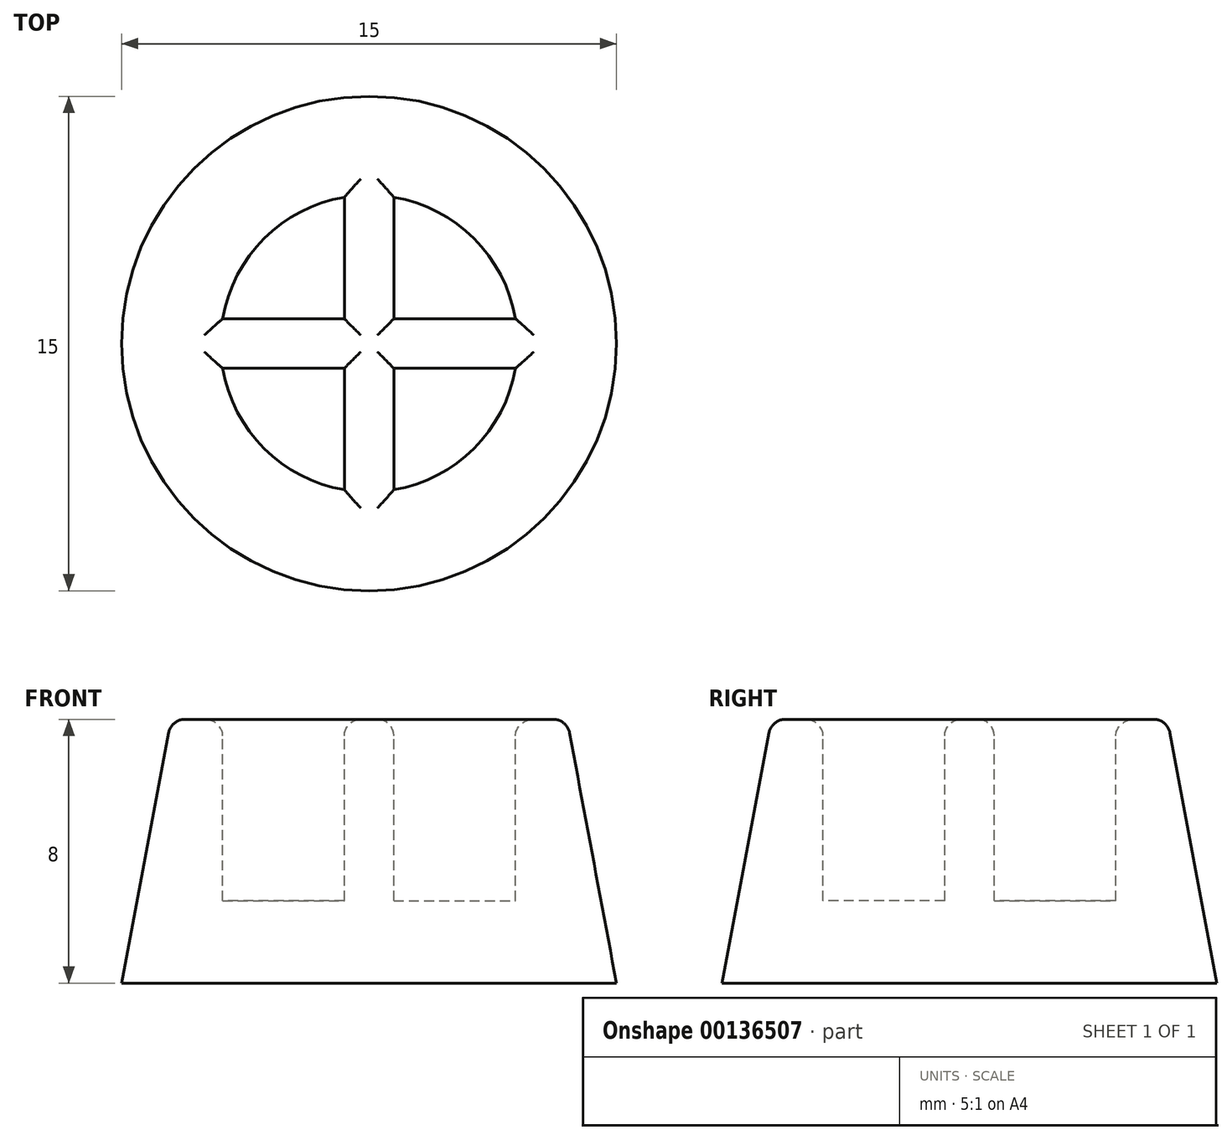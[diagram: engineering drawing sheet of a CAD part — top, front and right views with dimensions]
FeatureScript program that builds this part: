
annotation { "Feature Type Name" : "Feature", "Feature Type Description" : "" }
export const myFeature = defineFeature(function(context is Context, id is Id, definition is map)
    precondition{}
    {
        {
            var Q0;
            Q0=qCreatedBy(makeId("Front.planeOp"),FACE);
            var sketch = newSketch(context, id + "F0", { "sketchPlane" : qUnion([Q0])});
            skLineSegment(sketch, "E0", {"start": v(0, 0) * mm, "end": v(7.5, 0) * mm});
            skLineSegment(sketch, "E1", {"start": v(7.5, 0) * mm, "end": v(6, 8) * mm});
            skLineSegment(sketch, "E2", {"start": v(6, 8) * mm, "end": v(4.5, 8) * mm});
            skLineSegment(sketch, "E3", {"start": v(4.5, 8) * mm, "end": v(4.5, 2.5) * mm});
            skLineSegment(sketch, "E4", {"start": v(4.5, 2.5) * mm, "end": v(0, 2.5) * mm});
            skLineSegment(sketch, "E5", {"start": v(0, 2.5) * mm, "end": v(0, 0) * mm});
            skSolve(sketch);
        }
        {
            var Q0;
            Q0 = qSketchRegion(id + "F0", true);
            var Q1;
            Q1=sQuery(id+"F0.wireOp",EDGE,"E5");
            revolve(context, id + "F1", {"entities" : qUnion([Q0]), "axis" : qUnion([Q1]), "revolveType" : RevolveType.FULL});
        }
        {
            var Q0;
            Q0=makeQuery(id+"F1.opRevolve","SWEPT_FACE",FACE,{"disambiguationData":[OSD([sQuery(id+"F0.wireOp",EDGE,"E4")])]});
            var sketch = newSketch(context, id + "F2", { "sketchPlane" : qUnion([Q0])});
            skLineSegment(sketch, "E6", {"start": v(-5, 0.75) * mm, "end": v(-0.75, 0.75) * mm});
            skLineSegment(sketch, "E7", {"start": v(-0.75, 0.75) * mm, "end": v(-0.75, 5) * mm});
            skLineSegment(sketch, "E8", {"start": v(-0.75, 5) * mm, "end": v(0.75, 5) * mm});
            skLineSegment(sketch, "E9", {"start": v(0.75, 5) * mm, "end": v(0.75, 0.75) * mm});
            skLineSegment(sketch, "E10", {"start": v(0.75, 0.75) * mm, "end": v(5, 0.75) * mm});
            skLineSegment(sketch, "E11", {"start": v(5, 0.75) * mm, "end": v(5, -0.75) * mm});
            skLineSegment(sketch, "E12", {"start": v(5, -0.75) * mm, "end": v(0.75, -0.75) * mm});
            skLineSegment(sketch, "E13", {"start": v(0.75, -0.75) * mm, "end": v(0.75, -5) * mm});
            skLineSegment(sketch, "E14", {"start": v(0.75, -5) * mm, "end": v(-0.75, -5) * mm});
            skLineSegment(sketch, "E15", {"start": v(-0.75, -5) * mm, "end": v(-0.75, -0.75) * mm});
            skLineSegment(sketch, "E16", {"start": v(-0.75, -0.75) * mm, "end": v(-5, -0.75) * mm});
            skLineSegment(sketch, "E17", {"start": v(-5, -0.75) * mm, "end": v(-5, 0.75) * mm});
            skLineSegment(sketch, "E18", {"start": v(-0.75, 5) * mm, "end": v(0.75, -5) * mm, "construction": true});
            skLineSegment(sketch, "E19", {"start": v(0.75, 5) * mm, "end": v(-0.75, -5) * mm, "construction": true});
            skPoint(sketch, "E20", {"position": v(0, 0) * mm});
            skSolve(sketch);
        }
        {
            var Q0;
            Q0 = qSketchRegion(id + "F2", true);
            var Q1;
            Q1=makeQuery(id+"F1.opRevolve","SWEPT_FACE",FACE,{"disambiguationData":[OSD([sQuery(id+"F0.wireOp",EDGE,"E2")])]});
            extrude(context, id + "F3", {"entities" : qUnion([Q0]), "operationType" : NewBodyOperationType.ADD, "endBound" : BoundingType.UP_TO_SURFACE, "endBoundEntityFace" : qUnion([Q1]), "depth" : 25 * mm});
        }
        {
            var Q0;
            Q0=makeQuery(id+"F1.opRevolve","SWEPT_EDGE",EDGE,{"disambiguationData":[OSD([sQuery(id+"F0.wireOp",EDGE,"E1"),sQuery(id+"F0.wireOp",EDGE,"E2")])]});
            var Q1;
            Q1=makeQuery(id+"F3.opExtrude","CAP_EDGE",EDGE,{"disambiguationData":[OSD([sQuery(id+"F2.wireOp",EDGE,"E16")])],"isStart":false});
            var Q2;
            Q2=makeQuery(id+"F3.opExtrude","CAP_EDGE",EDGE,{"disambiguationData":[OSD([sQuery(id+"F2.wireOp",EDGE,"E15")])],"isStart":false});
            var Q3;
            {var subQ0=sQuery(id+"F2.wireOp",EDGE,"E15");var subQ2=sQuery(id+"F0.wireOp",EDGE,"E3");var subQ3=sQuery(id+"F0.wireOp",EDGE,"E2");Q3=makeQuery(id+"F3.boolean.opBoolean","SPLIT",EDGE,{"disambiguationData":[TD([makeQuery(id+"F3.opExtrude","SWEPT_FACE",FACE,{"disambiguationData":[OSD([subQ0])]})])],"derivedFrom":makeQuery(id+"F1.opRevolve","SWEPT_EDGE",EDGE,{"disambiguationData":[OSD([subQ3,subQ2])]})});}
            var Q4;
            {var subQ1=sQuery(id+"F2.wireOp",EDGE,"E6");var subQ2=sQuery(id+"F0.wireOp",EDGE,"E3");var subQ3=sQuery(id+"F0.wireOp",EDGE,"E2");Q4=makeQuery(id+"F3.boolean.opBoolean","SPLIT",EDGE,{"disambiguationData":[TD([makeQuery(id+"F3.opExtrude","SWEPT_FACE",FACE,{"disambiguationData":[OSD([subQ1])]})])],"derivedFrom":makeQuery(id+"F1.opRevolve","SWEPT_EDGE",EDGE,{"disambiguationData":[OSD([subQ3,subQ2])]})});}
            var Q5;
            Q5=makeQuery(id+"F3.opExtrude","CAP_EDGE",EDGE,{"disambiguationData":[OSD([sQuery(id+"F2.wireOp",EDGE,"E6")])],"isStart":false});
            var Q6;
            Q6=makeQuery(id+"F3.opExtrude","CAP_EDGE",EDGE,{"disambiguationData":[OSD([sQuery(id+"F2.wireOp",EDGE,"E7")])],"isStart":false});
            var Q7;
            Q7=makeQuery(id+"F3.opExtrude","CAP_EDGE",EDGE,{"disambiguationData":[OSD([sQuery(id+"F2.wireOp",EDGE,"E9")])],"isStart":false});
            var Q8;
            {var subQ1=sQuery(id+"F2.wireOp",EDGE,"E9");var subQ2=sQuery(id+"F0.wireOp",EDGE,"E3");var subQ3=sQuery(id+"F0.wireOp",EDGE,"E2");Q8=makeQuery(id+"F3.boolean.opBoolean","SPLIT",EDGE,{"disambiguationData":[TD([makeQuery(id+"F3.opExtrude","SWEPT_FACE",FACE,{"disambiguationData":[OSD([subQ1])]})])],"derivedFrom":makeQuery(id+"F1.opRevolve","SWEPT_EDGE",EDGE,{"disambiguationData":[OSD([subQ3,subQ2])]})});}
            var Q9;
            Q9=makeQuery(id+"F3.opExtrude","CAP_EDGE",EDGE,{"disambiguationData":[OSD([sQuery(id+"F2.wireOp",EDGE,"E10")])],"isStart":false});
            var Q10;
            Q10=makeQuery(id+"F3.opExtrude","CAP_EDGE",EDGE,{"disambiguationData":[OSD([sQuery(id+"F2.wireOp",EDGE,"E12")])],"isStart":false});
            var Q11;
            {var subQ0=sQuery(id+"F2.wireOp",EDGE,"E12");var subQ2=sQuery(id+"F0.wireOp",EDGE,"E3");var subQ3=sQuery(id+"F0.wireOp",EDGE,"E2");Q11=makeQuery(id+"F3.boolean.opBoolean","SPLIT",EDGE,{"disambiguationData":[TD([makeQuery(id+"F3.opExtrude","SWEPT_FACE",FACE,{"disambiguationData":[OSD([subQ0])]})])],"derivedFrom":makeQuery(id+"F1.opRevolve","SWEPT_EDGE",EDGE,{"disambiguationData":[OSD([subQ3,subQ2])]})});}
            var Q12;
            Q12=makeQuery(id+"F3.opExtrude","CAP_EDGE",EDGE,{"disambiguationData":[OSD([sQuery(id+"F2.wireOp",EDGE,"E13")])],"isStart":false});
            fillet(context, id + "F4", {"entities" : qUnion([Q0, Q1, Q2, Q3, Q4, Q5, Q6, Q7, Q8, Q9, Q10, Q11, Q12]), "radius" : 0.5 * mm, "tangentPropagation" : true, "allowEdgeOverflow" : false});
        }
    });
